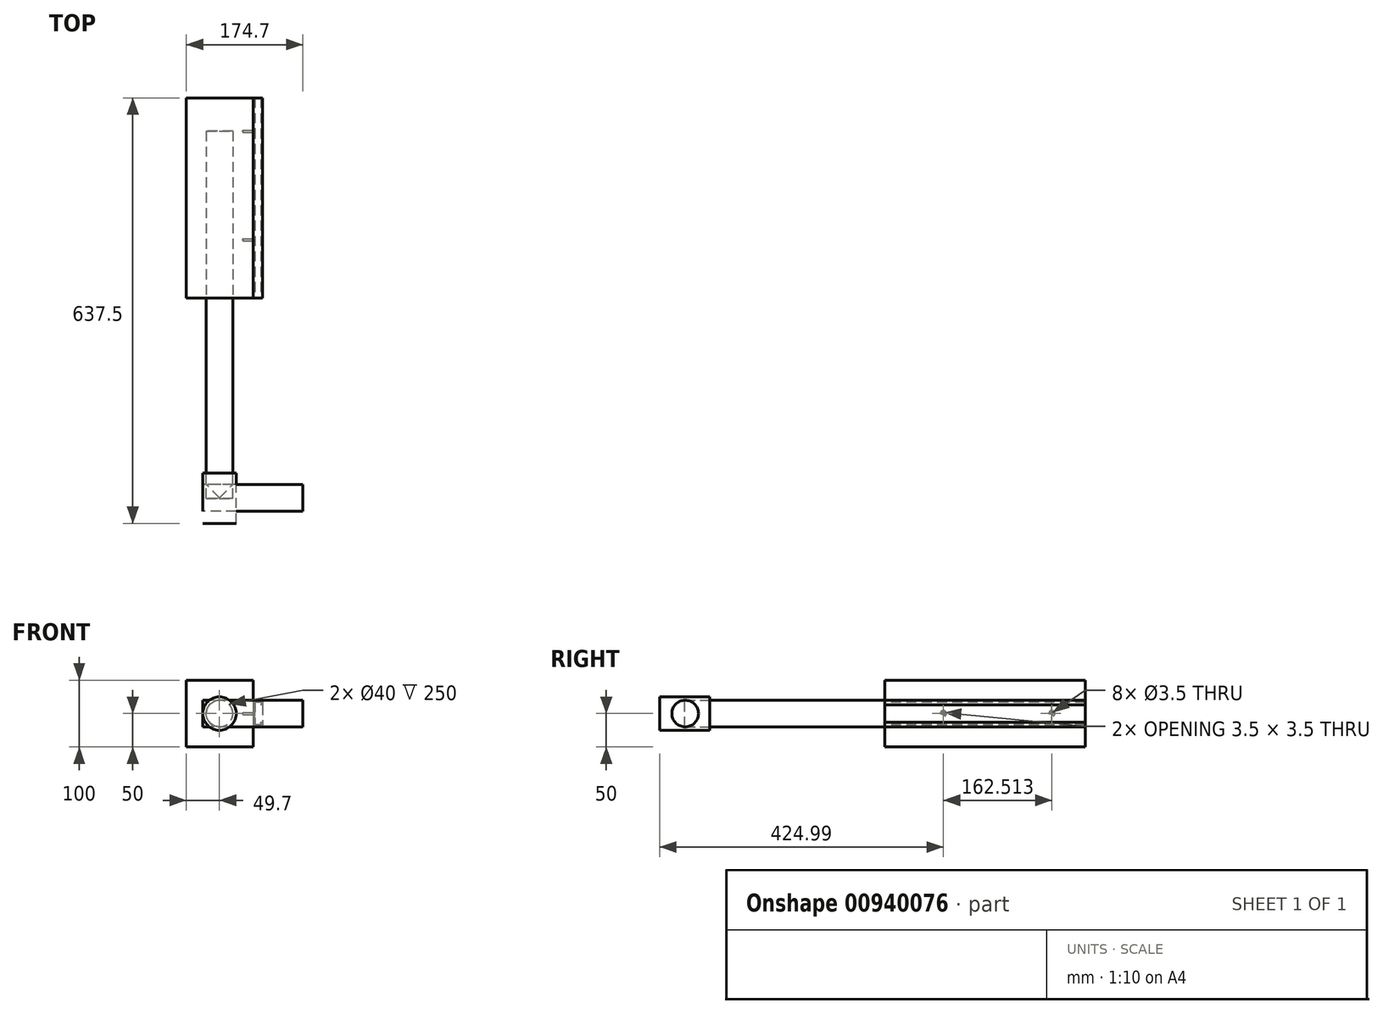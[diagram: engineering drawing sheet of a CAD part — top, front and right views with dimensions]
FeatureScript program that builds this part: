
annotation { "Feature Type Name" : "Feature", "Feature Type Description" : "" }
export const myFeature = defineFeature(function(context is Context, id is Id, definition is map)
    precondition{}
    {
        {
            var Q0;
            Q0=qCreatedBy(makeId("Top.planeOp"),FACE);
            var sketch = newSketch(context, id + "F0", { "sketchPlane" : qUnion([Q0])});
            skLineSegment(sketch, "E0.bottom", {"start": v(-49.7, 212.51) * mm, "end": v(50.3, 212.51) * mm});
            skLineSegment(sketch, "E0.top", {"start": v(-49.7, -87.49) * mm, "end": v(50.3, -87.49) * mm});
            skLineSegment(sketch, "E0.left", {"start": v(-49.7, 212.51) * mm, "end": v(-49.7, -87.49) * mm});
            skLineSegment(sketch, "E0.right", {"start": v(50.3, 212.51) * mm, "end": v(50.3, -87.49) * mm});
            skSolve(sketch);
        }
        {
            var Q0;
            Q0 = qSketchRegion(id + "F0", true);
            extrude(context, id + "F1", {"entities" : qUnion([Q0]), "endBound" : BoundingType.SYMMETRIC, "depth" : 100 * mm, "offsetDistance" : 25 * mm});
        }
        {
            var Q0;
            Q0=makeQuery(id+"F1.opExtrude","SWEPT_FACE",FACE,{"disambiguationData":[OSD([sQuery(id+"F0.wireOp",EDGE,"E0.top")])]});
            var sketch = newSketch(context, id + "F2", { "sketchPlane" : qUnion([Q0])});
            skCircle(sketch, "E1", {"center": v(0, 0) * mm, "radius": 20 * mm});
            skSolve(sketch);
        }
        {
            var Q0;
            Q0 = qSketchRegion(id + "F2", true);
            extrude(context, id + "F3", {"entities" : qUnion([Q0]), "operationType" : NewBodyOperationType.REMOVE, "oppositeDirection" : true, "depth" : 250 * mm, "offsetDistance" : 25 * mm});
        }
        {
            var Q0;
            Q0 = qSketchRegion(id + "F2", true);
            extrude(context, id + "F4", {"entities" : qUnion([Q0]), "depth" : 300 * mm, "offsetDistance" : 25 * mm});
        }
        {
            var Q0;
            Q0=makeQuery(id+"F4.opExtrude","CAP_FACE",FACE,{"disambiguationData":[OSD([sQuery(id+"F2.wireOp",EDGE,"E1")])],"isStart":false});
            var sketch = newSketch(context, id + "F5", { "sketchPlane" : qUnion([Q0])});
            skCircle(sketch, "E2", {"center": v(0, 0) * mm, "radius": 25 * mm});
            skSolve(sketch);
        }
        {
            var Q0;
            Q0 = qSketchRegion(id + "F5", true);
            extrude(context, id + "F6", {"entities" : qUnion([Q0]), "endBound" : BoundingType.SYMMETRIC, "depth" : 75 * mm, "offsetDistance" : 25 * mm});
        }
        {
            var Q0;
            Q0=makeQuery(id+"F4.opExtrude","SWEPT_BODY",BODY,{"disambiguationData":[OSD([sQuery(id+"F2.wireOp",EDGE,"E1")])]});
            var Q1;
            Q1=makeQuery(id+"F6.opExtrude","SWEPT_BODY",BODY,{"disambiguationData":[OSD([sQuery(id+"F5.wireOp",EDGE,"E2")])]});
            booleanBodies(context, id + "F7", {"operationType" : BooleanOperationType.INTERSECTION, "tools" : qUnion([Q0, Q1]), "keepTools" : true});
        }
        {
            var Q0;
            Q0=qCreatedBy(makeId("Right.planeOp"),FACE);
            var sketch = newSketch(context, id + "F8", { "sketchPlane" : qUnion([Q0])});
            skPoint(sketch, "E3", {"position": v(-386.7, 0) * mm});
            skCircle(sketch, "E4", {"center": v(-386.7, 0) * mm, "radius": 20 * mm});
            skSolve(sketch);
        }
        {
            var Q0;
            Q0 = qSketchRegion(id + "F8", true);
            extrude(context, id + "F9", {"entities" : qUnion([Q0]), "endBound" : BoundingType.SYMMETRIC, "depth" : 100 * mm, "offsetDistance" : 25 * mm});
        }
        {
            var Q0;
            Q0=makeQuery(id+"F9.opExtrude","SWEPT_BODY",BODY,{"disambiguationData":[OSD([sQuery(id+"F8.wireOp",EDGE,"E4")])]});
            var Q1;
            Q1=makeQuery(id+"F4.opExtrude","SWEPT_BODY",BODY,{"disambiguationData":[OSD([sQuery(id+"F2.wireOp",EDGE,"E1")])]});
            booleanBodies(context, id + "F10", {"operationType" : BooleanOperationType.SUBTRACTION, "tools" : qUnion([Q0]), "targets" : qUnion([Q1])});
        }
        {
            var Q0;
            Q0 = qSketchRegion(id + "F8", true);
            extrude(context, id + "F11", {"entities" : qUnion([Q0]), "endBound" : BoundingType.SYMMETRIC, "depth" : 150 * mm, "offsetDistance" : 25 * mm});
        }
        {
            var Q0;
            Q0=makeQuery(id+"F11.opExtrude","SWEPT_BODY",BODY,{"disambiguationData":[OSD([sQuery(id+"F8.wireOp",EDGE,"E4")])]});
            transform(context, id + "F12", {"entities" : qUnion([Q0]), "transformType" : TransformType.TRANSLATION_3D, "dx" : 50 * mm, "dy" : 0 * mm, "dz" : 0 * mm, "makeCopy" : true});
        }
        {
            var Q0;
            Q0=makeQuery(id+"F11.opExtrude","SWEPT_BODY",BODY,{"disambiguationData":[OSD([sQuery(id+"F8.wireOp",EDGE,"E4")])]});
            deleteBodies(context, id + "F13", {"entities" : qUnion([Q0])});
        }
        {
            var Q0;
            Q0=makeQuery(id+"F1.opExtrude","SWEPT_FACE",FACE,{"disambiguationData":[OSD([sQuery(id+"F0.wireOp",EDGE,"E0.bottom")])]});
            var sketch = newSketch(context, id + "F14", { "sketchPlane" : qUnion([Q0])});
            skLineSegment(sketch, "E5.bottom", {"start": v(-50.3, 20) * mm, "end": v(-64.75, 20) * mm});
            skLineSegment(sketch, "E5.top", {"start": v(-50.3, -20) * mm, "end": v(-64.75, -20) * mm});
            skLineSegment(sketch, "E5.left", {"start": v(-50.3, 20) * mm, "end": v(-50.3, -20) * mm});
            skLineSegment(sketch, "E5.right", {"start": v(-64.75, 20) * mm, "end": v(-64.75, 13) * mm});
            skPoint(sketch, "E6", {"position": v(-64.75, 13) * mm});
            skPoint(sketch, "E7", {"position": v(-61.75, 13) * mm});
            skPoint(sketch, "E8", {"position": v(-62.3, 16.96) * mm});
            skPoint(sketch, "E9", {"position": v(-53.3, 16.96) * mm});
            skPoint(sketch, "E10", {"position": v(-53.3, -17) * mm});
            skPoint(sketch, "E11", {"position": v(-62.3, -17) * mm});
            skPoint(sketch, "E12", {"position": v(-61.75, -13) * mm});
            skPoint(sketch, "E13", {"position": v(-64.75, -13) * mm});
            skLineSegment(sketch, "E14", {"start": v(-64.75, 13) * mm, "end": v(-61.75, 13) * mm});
            skLineSegment(sketch, "E15", {"start": v(-62.3, 16.96) * mm, "end": v(-61.75, 13) * mm});
            skLineSegment(sketch, "E16", {"start": v(-62.3, 16.96) * mm, "end": v(-53.3, 16.96) * mm});
            skLineSegment(sketch, "E17", {"start": v(-53.3, 16.96) * mm, "end": v(-53.3, -17) * mm});
            skLineSegment(sketch, "E18", {"start": v(-62.3, -17) * mm, "end": v(-53.3, -17) * mm});
            skLineSegment(sketch, "E19", {"start": v(-62.3, -17) * mm, "end": v(-61.75, -13) * mm});
            skLineSegment(sketch, "E20", {"start": v(-61.75, -13) * mm, "end": v(-64.75, -13) * mm});
            skLineSegment(sketch, "E21.trimOffspring", {"start": v(-64.75, -13) * mm, "end": v(-64.75, -20) * mm});
            skSolve(sketch);
        }
        {
            var Q0;
            Q0=makeQuery(id+"F1.opExtrude","SWEPT_FACE",FACE,{"disambiguationData":[OSD([sQuery(id+"F0.wireOp",EDGE,"E0.right")])]});
            var sketch = newSketch(context, id + "F15", { "sketchPlane" : qUnion([Q0])});
            skLineSegment(sketch, "E22", {"start": v(-87.49, 0) * mm, "end": v(212.51, 0) * mm});
            skSolve(sketch);
        }
        {
            var Q0;
            Q0=makeQuery(id+"F14.imprint","IMPRINT",FACE,{"disambiguationData":[TD([[makeQuery(id+"F14.imprint","IMPRINT",EDGE,{"derivedFrom":sQuery(id+"F14.wireOp",EDGE,"E5.bottom")}),1.0]])]});
            var Q1;
            Q1=sQuery(id+"F15.wireOp",EDGE,"E22");
            sweep(context, id + "F16", {"profiles" : qUnion([Q0]), "path" : qUnion([Q1])});
        }
        {
            var Q0;
            Q0=makeQuery(id+"F16.opSweep","SWEPT_FACE",FACE,{"disambiguationData":[OSD([sQuery(id+"F14.wireOp",EDGE,"E17"),sQuery(id+"F15.wireOp",EDGE,"E22")])]});
            var sketch = newSketch(context, id + "F17", { "sketchPlane" : qUnion([Q0])});
            skPoint(sketch, "E23", {"position": v(0, 0) * mm});
            skPoint(sketch, "E24", {"position": v(162.51, 0) * mm});
            skSolve(sketch);
        }
        {
            var Q0;
            Q0=sQuery(id+"F17.wireOp",VERTEX,"E24");
            var Q1;
            Q1=sQuery(id+"F17.wireOp",VERTEX,"E23");
            var Q2;
            Q2=makeQuery(id+"F1.opExtrude","SWEPT_BODY",BODY,{"disambiguationData":[OSD([sQuery(id+"F0.wireOp",EDGE,"E0.bottom"),sQuery(id+"F0.wireOp",EDGE,"E0.top"),sQuery(id+"F0.wireOp",EDGE,"E0.left"),sQuery(id+"F0.wireOp",EDGE,"E0.right")])]});
            var Q3;
            Q3=makeQuery(id+"F16.opSweep","SWEPT_BODY",BODY,{"disambiguationData":[OSD([sQuery(id+"F14.wireOp",EDGE,"E5.bottom"),sQuery(id+"F14.wireOp",EDGE,"E5.top"),sQuery(id+"F14.wireOp",EDGE,"E5.left"),sQuery(id+"F14.wireOp",EDGE,"E5.right"),sQuery(id+"F14.wireOp",EDGE,"E14"),sQuery(id+"F14.wireOp",EDGE,"E15"),sQuery(id+"F14.wireOp",EDGE,"E16"),sQuery(id+"F14.wireOp",EDGE,"E17"),sQuery(id+"F14.wireOp",EDGE,"E18"),sQuery(id+"F14.wireOp",EDGE,"E19"),sQuery(id+"F14.wireOp",EDGE,"E20"),sQuery(id+"F14.wireOp",EDGE,"E21.trimOffspring"),sQuery(id+"F15.wireOp",EDGE,"E22")])]});
            hole(context, id + "F18", {"style" : HoleStyle.C_SINK, "endStyle" : HoleEndStyle.BLIND, "standardTappedOrClearance" : lookupTablePath({ "standard" : "ISO", "engagement" : "75%", "pitch" : "0.5 mm", "size" : "M4", "type" : "Tapped" }), "standardBlindInLast" : lookupTablePath({ "standard" : "ISO", "fit" : "Normal", "engagement" : "75%", "pitch" : "0.5 mm", "size" : "M4", "type" : "Clearance & tapped" }), "holeDiameter" : 3.5 * mm, "cSinkDiameter" : 8.96 * mm, "cSinkAngle" : 90 * degree, "majorDiameter" : 4 * mm, "showTappedDepth" : true, "holeDepth" : 18 * mm, "isTappedThrough" : true, "tappedDepth" : 12 * mm, "tapClearance" : 12, "locations" : qUnion([Q0, Q1]), "scope" : qUnion([Q2, Q3])});
        }
        {
            var Q0;
            Q0=makeQuery(id+"F16.opSweep","CAP_FACE",FACE,{"disambiguationData":[OSD([sQuery(id+"F14.wireOp",EDGE,"E5.bottom"),sQuery(id+"F14.wireOp",EDGE,"E5.top"),sQuery(id+"F14.wireOp",EDGE,"E5.left"),sQuery(id+"F14.wireOp",EDGE,"E5.right"),sQuery(id+"F14.wireOp",EDGE,"E14"),sQuery(id+"F14.wireOp",EDGE,"E15"),sQuery(id+"F14.wireOp",EDGE,"E16"),sQuery(id+"F14.wireOp",EDGE,"E17"),sQuery(id+"F14.wireOp",EDGE,"E18"),sQuery(id+"F14.wireOp",EDGE,"E19"),sQuery(id+"F14.wireOp",EDGE,"E20"),sQuery(id+"F14.wireOp",EDGE,"E21.trimOffspring"),sQuery(id+"F15.wireOp",VERTEX,"E22.end")])],"isStart":true});
            var sketch = newSketch(context, id + "F19", { "sketchPlane" : qUnion([Q0])});
            skPoint(sketch, "E25", {"position": v(-64.75, 13) * mm});
            skPoint(sketch, "E26", {"position": v(-61.75, 13) * mm});
            skPoint(sketch, "E27", {"position": v(-62.3, 16.96) * mm});
            skPoint(sketch, "E28", {"position": v(-53.3, 16.96) * mm});
            skPoint(sketch, "E29", {"position": v(-53.3, -17) * mm});
            skPoint(sketch, "E30", {"position": v(-62.3, -17) * mm});
            skPoint(sketch, "E31", {"position": v(-61.75, -13) * mm});
            skPoint(sketch, "E32", {"position": v(-64.75, -13) * mm});
            skLineSegment(sketch, "E33", {"start": v(-64.75, 13) * mm, "end": v(-64.75, -13) * mm});
            skLineSegment(sketch, "E34", {"start": v(-61.75, -13) * mm, "end": v(-62.3, -17) * mm});
            skLineSegment(sketch, "E35", {"start": v(-53.3, -17) * mm, "end": v(-53.3, 16.96) * mm});
            skLineSegment(sketch, "E36", {"start": v(-62.3, 16.96) * mm, "end": v(-53.3, 16.96) * mm});
            skSolve(sketch);
        }
        {
            var Q0;
            Q0=makeQuery(id+"F16.opSweep","SWEPT_FACE",FACE,{"disambiguationData":[OSD([sQuery(id+"F14.wireOp",EDGE,"E17"),sQuery(id+"F15.wireOp",EDGE,"E22")])]});
            var sketch = newSketch(context, id + "F20", { "sketchPlane" : qUnion([Q0])});
            skLineSegment(sketch, "E37", {"start": v(-87.49, 0) * mm, "end": v(212.51, -0.02) * mm});
            skPoint(sketch, "E37.startSnap0", {"position": v(-87.49, -0.02) * mm});
            skSolve(sketch);
        }
        {
            var Q0;
            Q0=makeQuery(id+"F19.imprint","IMPRINT",FACE,{"disambiguationData":[TD([[makeQuery(id+"F19.imprint","IMPRINT",EDGE,{"derivedFrom":sQuery(id+"F19.wireOp",EDGE,"E33")}),1.0]])]});
            var Q1;
            Q1=sQuery(id+"F20.wireOp",EDGE,"E37");
            sweep(context, id + "F21", {"profiles" : qUnion([Q0]), "path" : qUnion([Q1])});
        }
    });
